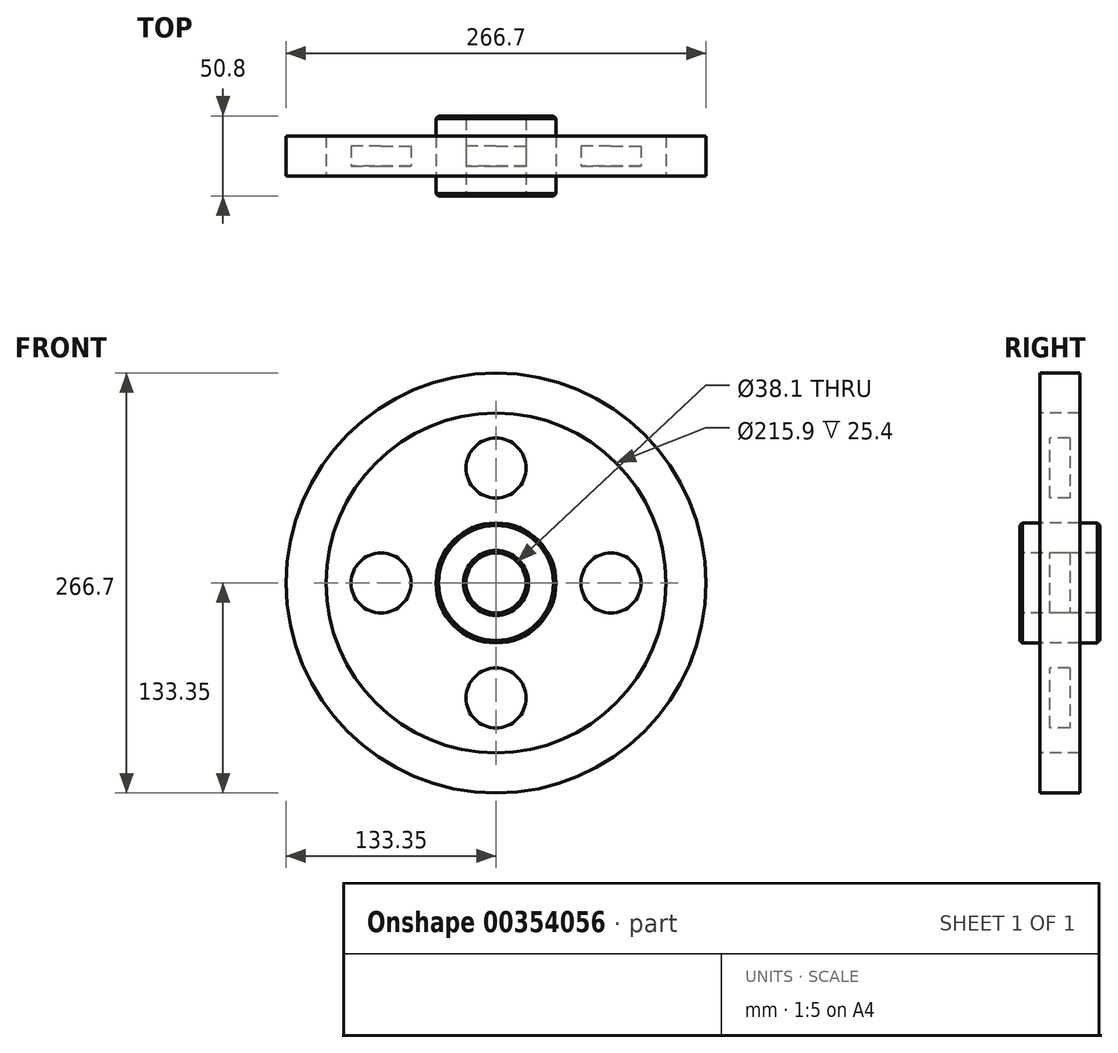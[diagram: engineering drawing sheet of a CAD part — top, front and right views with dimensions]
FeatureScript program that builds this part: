
annotation { "Feature Type Name" : "Feature", "Feature Type Description" : "" }
export const myFeature = defineFeature(function(context is Context, id is Id, definition is map)
    precondition{}
    {
        {
            var Q0;
            Q0=qCreatedBy(makeId("Right.planeOp"),FACE);
            var sketch = newSketch(context, id + "F0", { "sketchPlane" : qUnion([Q0])});
            skLineSegment(sketch, "E0", {"start": v(0, 0) * mm, "end": v(77.42, 0) * mm, "construction": true});
            skLineSegment(sketch, "E1.0", {"start": v(0, 19.05) * mm, "end": v(25.4, 19.05) * mm});
            skLineSegment(sketch, "E2.0", {"start": v(6.35, 38.1) * mm, "end": v(25.4, 38.1) * mm});
            skLineSegment(sketch, "E3.0", {"start": v(6.35, 107.95) * mm, "end": v(12.7, 107.95) * mm});
            skLineSegment(sketch, "E4.0", {"start": v(0, 133.35) * mm, "end": v(12.7, 133.35) * mm});
            skLineSegment(sketch, "E5", {"start": v(0, 19.05) * mm, "end": v(0, 133.35) * mm, "construction": true});
            skLineSegment(sketch, "E6.0", {"start": v(25.4, 19.05) * mm, "end": v(25.4, 38.1) * mm});
            skLineSegment(sketch, "E7", {"start": v(12.7, 133.35) * mm, "end": v(12.7, 107.95) * mm});
            skLineSegment(sketch, "E8", {"start": v(25.4, 19.05) * mm, "end": v(0, 19.05) * mm});
            skLineSegment(sketch, "E9.trimOffspring", {"start": v(12.7, 107.95) * mm, "end": v(12.7, 133.35) * mm});
            skPoint(sketch, "E10.orphan", {"position": v(25.4, 107.95) * mm});
            skPoint(sketch, "E11.orphan", {"position": v(6.35, 107.95) * mm});
            skLineSegment(sketch, "E12", {"start": v(6.35, 107.95) * mm, "end": v(6.35, 38.1) * mm});
            skPoint(sketch, "E13.orphan", {"position": v(0, 107.95) * mm});
            skLineSegment(sketch, "E14.MirrorCS", {"start": v(0, 133.35) * mm, "end": v(-12.7, 133.35) * mm});
            skLineSegment(sketch, "E15.MirrorCS", {"start": v(-12.7, 107.95) * mm, "end": v(-12.7, 133.35) * mm});
            skPoint(sketch, "E16.MirrorP", {"position": v(-6.35, 107.95) * mm});
            skLineSegment(sketch, "E17.MirrorCS", {"start": v(-6.35, 107.95) * mm, "end": v(-6.35, 38.1) * mm});
            skLineSegment(sketch, "E18.MirrorCS", {"start": v(-6.35, 38.1) * mm, "end": v(-25.4, 38.1) * mm});
            skLineSegment(sketch, "E19.MirrorCS", {"start": v(-25.4, 19.05) * mm, "end": v(-25.4, 38.1) * mm});
            skLineSegment(sketch, "E20.MirrorCS", {"start": v(-25.4, 19.05) * mm, "end": v(0, 19.05) * mm});
            skLineSegment(sketch, "E21", {"start": v(-12.7, 107.95) * mm, "end": v(-6.35, 107.95) * mm});
            skSolve(sketch);
        }
        {
            var Q0;
            Q0=makeQuery(id+"F0.imprint","IMPRINT",FACE,{"disambiguationData":[TD([[makeQuery(id+"F0.imprint","IMPRINT",EDGE,{"derivedFrom":sQuery(id+"F0.wireOp",EDGE,"E3.0")}),1.0]])]});
            var Q1;
            Q1=sQuery(id+"F0.wireOp",EDGE,"E0");
            revolve(context, id + "F1", {"entities" : qUnion([Q0]), "axis" : qUnion([Q1]), "revolveType" : RevolveType.FULL});
        }
        {
            var Q0;
            Q0=makeQuery(id+"F1.opRevolve","SWEPT_FACE",FACE,{"disambiguationData":[OSD([sQuery(id+"F0.wireOp",EDGE,"E17.MirrorCS")])]});
            var sketch = newSketch(context, id + "F2", { "sketchPlane" : qUnion([Q0])});
            skLineSegment(sketch, "E22", {"start": v(0, 0) * mm, "end": v(0, 73.03) * mm});
            skCircle(sketch, "E23", {"center": v(0, 73.03) * mm, "radius": 19.05 * mm});
            skCircle(sketch, "E24.1.0", {"center": v(-73.03, 0) * mm, "radius": 19.05 * mm});
            skCircle(sketch, "E24.2.0", {"center": v(0, -73.03) * mm, "radius": 19.05 * mm});
            skCircle(sketch, "E24.3.0", {"center": v(73.03, 0) * mm, "radius": 19.05 * mm});
            skPoint(sketch, "E24.center", {"position": v(0, 0) * mm});
            skSolve(sketch);
        }
        {
            var Q0;
            Q0=makeQuery(id+"F2.imprint","IMPRINT",FACE,{"disambiguationData":[TD([[makeQuery(id+"F2.imprint","IMPRINT",EDGE,{"derivedFrom":sQuery(id+"F2.wireOp",EDGE,"E24.1.0")}),-1.0]])]});
            var Q1;
            Q1=makeQuery(id+"F2.imprint","IMPRINT",FACE,{"disambiguationData":[TD([[makeQuery(id+"F2.imprint","IMPRINT",EDGE,{"derivedFrom":sQuery(id+"F2.wireOp",EDGE,"E23")}),-1.0]])]});
            var Q2;
            Q2=makeQuery(id+"F2.imprint","IMPRINT",FACE,{"disambiguationData":[TD([[makeQuery(id+"F2.imprint","IMPRINT",EDGE,{"derivedFrom":sQuery(id+"F2.wireOp",EDGE,"E24.3.0")}),-1.0]])]});
            var Q3;
            Q3=makeQuery(id+"F2.imprint","IMPRINT",FACE,{"disambiguationData":[TD([[makeQuery(id+"F2.imprint","IMPRINT",EDGE,{"derivedFrom":sQuery(id+"F2.wireOp",EDGE,"E24.2.0")}),-1.0]])]});
            extrude(context, id + "F3", {"entities" : qUnion([Q0, Q1, Q2, Q3]), "operationType" : NewBodyOperationType.REMOVE, "oppositeDirection" : true, "depth" : 25.4 * mm});
        }
        {
            var Q0;
            Q0=makeQuery(id+"F1.opRevolve","SWEPT_FACE",FACE,{"disambiguationData":[OSD([sQuery(id+"F0.wireOp",EDGE,"E19.MirrorCS")])]});
            var Q1;
            Q1=makeQuery(id+"F1.opRevolve","SWEPT_FACE",FACE,{"disambiguationData":[OSD([sQuery(id+"F0.wireOp",EDGE,"E6.0")])]});
            chamfer(context, id + "F4", {"entities" : qUnion([Q0, Q1]), "width" : 1.59 * mm, "tangentPropagation" : true});
        }
    });
